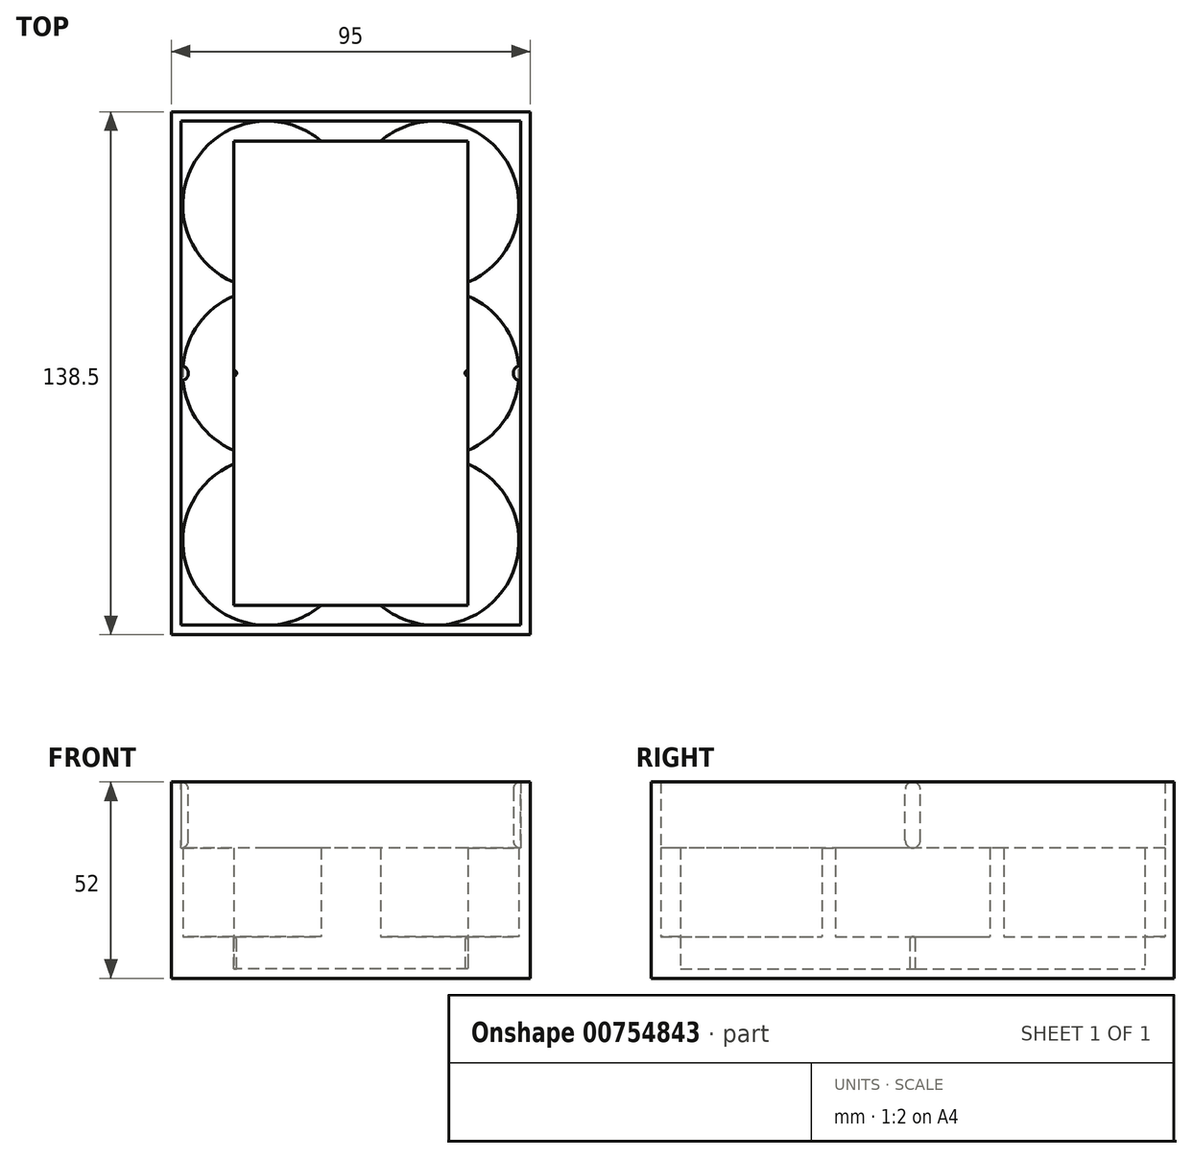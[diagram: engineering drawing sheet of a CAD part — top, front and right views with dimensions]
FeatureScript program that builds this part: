
annotation { "Feature Type Name" : "Feature", "Feature Type Description" : "" }
export const myFeature = defineFeature(function(context is Context, id is Id, definition is map)
    precondition{}
    {
        {
            var Q0;
            Q0=qCreatedBy(makeId("Top.planeOp"),FACE);
            var sketch = newSketch(context, id + "F0", { "sketchPlane" : qUnion([Q0])});
            skLineSegment(sketch, "E0.rect.bottom", {"start": v(47.5, 69.25) * mm, "end": v(-47.5, 69.25) * mm});
            skLineSegment(sketch, "E0.rect.top", {"start": v(47.5, -69.25) * mm, "end": v(-47.5, -69.25) * mm});
            skLineSegment(sketch, "E0.rect.left", {"start": v(47.5, 69.25) * mm, "end": v(47.5, -69.25) * mm});
            skLineSegment(sketch, "E0.rect.right", {"start": v(-47.5, 69.25) * mm, "end": v(-47.5, -69.25) * mm});
            skPoint(sketch, "E0.rect.middle", {"position": v(0, 0) * mm});
            skSolve(sketch);
        }
        {
            var Q0;
            Q0=qSketchRegion(id+"F0",true);
            extrude(context, id + "F1", {"entities" : qUnion([Q0]), "depth" : 2.5 * mm});
        }
        {
            var Q0;
            Q0=makeQuery(id+"F1.opExtrude","CAP_FACE",FACE,{"disambiguationData":[OSD([sQuery(id+"F0.wireOp",EDGE,"E0.rect.bottom"),sQuery(id+"F0.wireOp",EDGE,"E0.rect.top"),sQuery(id+"F0.wireOp",EDGE,"E0.rect.left"),sQuery(id+"F0.wireOp",EDGE,"E0.rect.right")])],"isStart":false});
            var sketch = newSketch(context, id + "F2", { "sketchPlane" : qUnion([Q0])});
            skLineSegment(sketch, "E1.rect.bottom", {"start": v(47.5, 69.25) * mm, "end": v(-47.5, 69.25) * mm});
            skLineSegment(sketch, "E1.rect.top", {"start": v(47.5, -69.25) * mm, "end": v(-47.5, -69.25) * mm});
            skLineSegment(sketch, "E1.rect.left", {"start": v(47.5, 69.25) * mm, "end": v(47.5, -69.25) * mm});
            skLineSegment(sketch, "E1.rect.right", {"start": v(-47.5, 69.25) * mm, "end": v(-47.5, -69.25) * mm});
            skPoint(sketch, "E1.rect.middle", {"position": v(0, 0) * mm});
            skLineSegment(sketch, "E2.rect.bottom", {"start": v(31, -61.5) * mm, "end": v(-31, -61.5) * mm});
            skLineSegment(sketch, "E2.rect.top", {"start": v(31, 61.5) * mm, "end": v(-31, 61.5) * mm});
            skLineSegment(sketch, "E2.rect.left", {"start": v(31, -61.5) * mm, "end": v(31, 61.5) * mm});
            skLineSegment(sketch, "E2.rect.right", {"start": v(-31, -61.5) * mm, "end": v(-31, 61.5) * mm});
            skSolve(sketch);
        }
        {
            var Q0;
            Q0=qSketchRegion(id+"F2",true);
            extrude(context, id + "F3", {"entities" : qUnion([Q0]), "operationType" : NewBodyOperationType.ADD, "depth" : 8.5 * mm});
        }
        {
            var Q0;
            Q0=makeQuery(id+"F3.opExtrude","CAP_FACE",FACE,{"disambiguationData":[OSD([sQuery(id+"F2.wireOp",EDGE,"E1.rect.bottom"),sQuery(id+"F2.wireOp",EDGE,"E1.rect.top"),sQuery(id+"F2.wireOp",EDGE,"E1.rect.left"),sQuery(id+"F2.wireOp",EDGE,"E1.rect.right"),sQuery(id+"F2.wireOp",EDGE,"E2.rect.bottom"),sQuery(id+"F2.wireOp",EDGE,"E2.rect.top"),sQuery(id+"F2.wireOp",EDGE,"E2.rect.left"),sQuery(id+"F2.wireOp",EDGE,"E2.rect.right")])],"isStart":false});
            var sketch = newSketch(context, id + "F4", { "sketchPlane" : qUnion([Q0])});
            skPoint(sketch, "E3.rect.middle", {"position": v(0, 0) * mm});
            skCircle(sketch, "E4", {"center": v(-22.25, 44.5) * mm, "radius": 22.25 * mm});
            skCircle(sketch, "E5", {"center": v(-22.25, -44.5) * mm, "radius": 22.25 * mm});
            skCircle(sketch, "E6", {"center": v(22.25, -44.5) * mm, "radius": 22.25 * mm});
            skCircle(sketch, "E7", {"center": v(22.25, 0) * mm, "radius": 22.25 * mm});
            skCircle(sketch, "E8", {"center": v(-22.25, 0) * mm, "radius": 22.25 * mm});
            skCircle(sketch, "E9", {"center": v(22.25, 44.5) * mm, "radius": 22.25 * mm});
            skLineSegment(sketch, "E10.rect.bottom", {"start": v(47.5, -69.25) * mm, "end": v(-47.5, -69.25) * mm});
            skLineSegment(sketch, "E10.rect.top", {"start": v(47.5, 69.25) * mm, "end": v(-47.5, 69.25) * mm});
            skLineSegment(sketch, "E10.rect.left", {"start": v(47.5, -69.25) * mm, "end": v(47.5, 69.25) * mm});
            skLineSegment(sketch, "E10.rect.right", {"start": v(-47.5, -69.25) * mm, "end": v(-47.5, 69.25) * mm});
            skLineSegment(sketch, "E11", {"start": v(-22.25, 44.5) * mm, "end": v(22.25, 44.5) * mm});
            skLineSegment(sketch, "E12", {"start": v(-22.25, 0) * mm, "end": v(22.25, 0) * mm});
            skLineSegment(sketch, "E13", {"start": v(-22.25, -44.5) * mm, "end": v(22.25, -44.5) * mm});
            skSolve(sketch);
        }
        {
            var Q0;
            Q0=qSketchRegion(id+"F4",true);
            extrude(context, id + "F5", {"entities" : qUnion([Q0]), "operationType" : NewBodyOperationType.ADD, "depth" : 23.5 * mm});
        }
        {
            var Q0;
            {var subQ0=sQuery(id+"F2.wireOp",EDGE,"E2.rect.top");var subQ1=sQuery(id+"F2.wireOp",EDGE,"E2.rect.right");var subQ2=sQuery(id+"F4.wireOp",EDGE,"E4");Q0=makeQuery(id+"F5.boolean.opBoolean","SPLIT",FACE,{"disambiguationData":[TD([makeQuery(id+"F5.opExtrude","SWEPT_FACE",FACE,{"disambiguationData":[OSD([subQ2])]})])],"derivedFrom":makeQuery(id+"F3.opExtrude","CAP_FACE",FACE,{"disambiguationData":[OSD([sQuery(id+"F2.wireOp",EDGE,"E1.rect.bottom"),sQuery(id+"F2.wireOp",EDGE,"E1.rect.top"),sQuery(id+"F2.wireOp",EDGE,"E1.rect.left"),sQuery(id+"F2.wireOp",EDGE,"E1.rect.right"),sQuery(id+"F2.wireOp",EDGE,"E2.rect.bottom"),subQ0,sQuery(id+"F2.wireOp",EDGE,"E2.rect.left"),subQ1])],"isStart":false})});}
            var sketch = newSketch(context, id + "F6", { "sketchPlane" : qUnion([Q0])});
            skLineSegment(sketch, "E14.rect.bottom", {"start": v(-31, 61.5) * mm, "end": v(31, 61.5) * mm});
            skLineSegment(sketch, "E14.rect.top", {"start": v(-31, -61.5) * mm, "end": v(31, -61.5) * mm});
            skLineSegment(sketch, "E14.rect.left", {"start": v(-31, 61.5) * mm, "end": v(-31, -61.5) * mm});
            skLineSegment(sketch, "E14.rect.right", {"start": v(31, 61.5) * mm, "end": v(31, -61.5) * mm});
            skPoint(sketch, "E14.rect.middle", {"position": v(0, 0) * mm});
            skSolve(sketch);
        }
        {
            var Q0;
            Q0=qSketchRegion(id+"F6",true);
            extrude(context, id + "F7", {"entities" : qUnion([Q0]), "operationType" : NewBodyOperationType.REMOVE, "endBound" : BoundingType.THROUGH_ALL, "depth" : 25 * mm});
        }
        {
            var Q0;
            Q0=makeQuery(id+"F5.opExtrude","CAP_FACE",FACE,{"disambiguationData":[OSD([sQuery(id+"F4.wireOp",EDGE,"E4"),sQuery(id+"F4.wireOp",EDGE,"E5"),sQuery(id+"F4.wireOp",EDGE,"E6"),sQuery(id+"F4.wireOp",EDGE,"E7"),sQuery(id+"F4.wireOp",EDGE,"E8"),sQuery(id+"F4.wireOp",EDGE,"E9"),sQuery(id+"F4.wireOp",EDGE,"E10.rect.bottom"),sQuery(id+"F4.wireOp",EDGE,"E10.rect.top"),sQuery(id+"F4.wireOp",EDGE,"E10.rect.left"),sQuery(id+"F4.wireOp",EDGE,"E10.rect.right")])],"isStart":false});
            var sketch = newSketch(context, id + "F8", { "sketchPlane" : qUnion([Q0])});
            skLineSegment(sketch, "E15.rect.bottom", {"start": v(47.5, 69.25) * mm, "end": v(-47.5, 69.25) * mm});
            skLineSegment(sketch, "E15.rect.top", {"start": v(47.5, -69.25) * mm, "end": v(-47.5, -69.25) * mm});
            skLineSegment(sketch, "E15.rect.left", {"start": v(47.5, 69.25) * mm, "end": v(47.5, -69.25) * mm});
            skLineSegment(sketch, "E15.rect.right", {"start": v(-47.5, 69.25) * mm, "end": v(-47.5, -69.25) * mm});
            skPoint(sketch, "E15.rect.middle", {"position": v(0, 0) * mm});
            skLineSegment(sketch, "E16.rect.bottom", {"start": v(45, 66.75) * mm, "end": v(-45, 66.75) * mm});
            skLineSegment(sketch, "E16.rect.top", {"start": v(45, -66.75) * mm, "end": v(-45, -66.75) * mm});
            skLineSegment(sketch, "E16.rect.left", {"start": v(45, 66.75) * mm, "end": v(45, -66.75) * mm});
            skLineSegment(sketch, "E16.rect.right", {"start": v(-45, 66.75) * mm, "end": v(-45, -66.75) * mm});
            skSolve(sketch);
        }
        {
            var Q0;
            Q0=qSketchRegion(id+"F8",true);
            extrude(context, id + "F9", {"entities" : qUnion([Q0]), "operationType" : NewBodyOperationType.ADD, "depth" : 17.5 * mm});
        }
        {
            var Q0;
            Q0=makeQuery(id+"F9.opExtrude","SWEPT_FACE",FACE,{"disambiguationData":[OSD([sQuery(id+"F8.wireOp",EDGE,"E16.rect.right")])]});
            var sketch = newSketch(context, id + "F10", { "sketchPlane" : qUnion([Q0])});
            skLineSegment(sketch, "E17", {"start": v(0, 34.5) * mm, "end": v(0, 52) * mm});
            skLineSegment(sketch, "E18", {"start": v(0, 52) * mm, "end": v(0, 50) * mm});
            skLineSegment(sketch, "E19", {"start": v(0, 34.5) * mm, "end": v(0, 36.5) * mm});
            skLineSegment(sketch, "E20", {"start": v(2, 50) * mm, "end": v(2, 36.5) * mm});
            skLineSegment(sketch, "E21", {"start": v(0, 52) * mm, "end": v(0, 34.5) * mm});
            skArc(sketch, "E22", {"start": v(2, 50) * mm, "mid": v(1.41, 51.41) * mm, "end": v(0, 52) * mm});
            skArc(sketch, "E23", {"start": v(0, 34.5) * mm, "mid": v(1.41, 35.09) * mm, "end": v(2, 36.5) * mm});
            skSolve(sketch);
        }
        {
            var Q0;
            Q0=qSketchRegion(id+"F10",true);
            var Q1;
            Q1=sQuery(id+"F10.wireOp",EDGE,"E21");
            revolve(context, id + "F11", {"operationType" : NewBodyOperationType.ADD, "entities" : qUnion([Q0]), "axis" : qUnion([Q1]), "revolveType" : RevolveType.ONE_DIRECTION, "angle" : 180 * degree});
        }
        {
            var Q0;
            Q0=makeQuery(id+"F9.opExtrude","SWEPT_FACE",FACE,{"disambiguationData":[OSD([sQuery(id+"F8.wireOp",EDGE,"E16.rect.left")])]});
            var sketch = newSketch(context, id + "F12", { "sketchPlane" : qUnion([Q0])});
            skLineSegment(sketch, "E24", {"start": v(0, 34.5) * mm, "end": v(0, 52) * mm});
            skLineSegment(sketch, "E25", {"start": v(0, 34.5) * mm, "end": v(0, 36.5) * mm});
            skLineSegment(sketch, "E26", {"start": v(0, 52) * mm, "end": v(0, 50) * mm});
            skLineSegment(sketch, "E27", {"start": v(-2, 36.5) * mm, "end": v(-2, 50) * mm});
            skLineSegment(sketch, "E28", {"start": v(0, 50) * mm, "end": v(-2, 50) * mm});
            skArc(sketch, "E29", {"start": v(0, 52) * mm, "mid": v(-1.41, 51.41) * mm, "end": v(-2, 50) * mm});
            skArc(sketch, "E30", {"start": v(-2, 36.5) * mm, "mid": v(-1.41, 35.09) * mm, "end": v(0, 34.5) * mm});
            skSolve(sketch);
        }
        {
            var Q0;
            Q0=qSketchRegion(id+"F12",true);
            var Q1;
            Q1=sQuery(id+"F12.wireOp",EDGE,"E24");
            revolve(context, id + "F13", {"operationType" : NewBodyOperationType.ADD, "entities" : qUnion([Q0]), "axis" : qUnion([Q1]), "revolveType" : RevolveType.ONE_DIRECTION, "angle" : 180 * degree});
        }
        {
            var Q0;
            Q0=makeQuery(id+"F7.boolean.opBoolean","MERGE",FACE,{"derivedFrom":[makeQuery(id+"F3.opExtrude","SWEPT_FACE",FACE,{"disambiguationData":[OSD([sQuery(id+"F2.wireOp",EDGE,"E2.rect.right")])]}),makeQuery(id+"F7.opExtrude","SWEPT_FACE",FACE,{"disambiguationData":[OSD([sQuery(id+"F6.wireOp",EDGE,"E14.rect.left")])]})]});
            var sketch = newSketch(context, id + "F14", { "sketchPlane" : qUnion([Q0])});
            skLineSegment(sketch, "E31", {"start": v(0, 11) * mm, "end": v(0, 2.5) * mm});
            skLineSegment(sketch, "E32", {"start": v(0, 2.5) * mm, "end": v(0.75, 2.5) * mm});
            skLineSegment(sketch, "E33", {"start": v(0, 11) * mm, "end": v(0, 10.25) * mm});
            skLineSegment(sketch, "E34", {"start": v(0, 10.25) * mm, "end": v(0.75, 10.25) * mm});
            skArc(sketch, "E35", {"start": v(0.75, 10.25) * mm, "mid": v(0.53, 10.78) * mm, "end": v(0, 11) * mm});
            skLineSegment(sketch, "E36", {"start": v(0.75, 10.25) * mm, "end": v(0.75, 2.5) * mm});
            skSolve(sketch);
        }
        {
            var Q0;
            Q0=qSketchRegion(id+"F14",true);
            var Q1;
            Q1=sQuery(id+"F14.wireOp",EDGE,"E31");
            revolve(context, id + "F15", {"operationType" : NewBodyOperationType.ADD, "entities" : qUnion([Q0]), "axis" : qUnion([Q1]), "revolveType" : RevolveType.FULL});
        }
        {
            var Q0;
            Q0=makeQuery(id+"F7.boolean.opBoolean","MERGE",FACE,{"derivedFrom":[makeQuery(id+"F3.opExtrude","SWEPT_FACE",FACE,{"disambiguationData":[OSD([sQuery(id+"F2.wireOp",EDGE,"E2.rect.left")])]}),makeQuery(id+"F7.opExtrude","SWEPT_FACE",FACE,{"disambiguationData":[OSD([sQuery(id+"F6.wireOp",EDGE,"E14.rect.right")])]})]});
            var sketch = newSketch(context, id + "F16", { "sketchPlane" : qUnion([Q0])});
            skLineSegment(sketch, "E37", {"start": v(0, 2.5) * mm, "end": v(0, 11) * mm});
            skLineSegment(sketch, "E38", {"start": v(0, 2.5) * mm, "end": v(-0.75, 2.5) * mm});
            skLineSegment(sketch, "E39", {"start": v(0, 11) * mm, "end": v(0, 10.25) * mm});
            skLineSegment(sketch, "E40", {"start": v(0, 10.25) * mm, "end": v(-0.75, 10.25) * mm});
            skArc(sketch, "E41", {"start": v(0, 11) * mm, "mid": v(-0.53, 10.78) * mm, "end": v(-0.75, 10.25) * mm});
            skLineSegment(sketch, "E42", {"start": v(-0.75, 2.5) * mm, "end": v(-0.75, 10.25) * mm});
            skSolve(sketch);
        }
        {
            var Q0;
            Q0=qSketchRegion(id+"F16",true);
            var Q1;
            Q1=sQuery(id+"F16.wireOp",EDGE,"E37");
            revolve(context, id + "F17", {"operationType" : NewBodyOperationType.ADD, "entities" : qUnion([Q0]), "axis" : qUnion([Q1]), "revolveType" : RevolveType.FULL});
        }
    });
